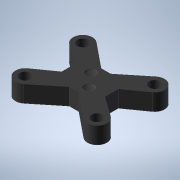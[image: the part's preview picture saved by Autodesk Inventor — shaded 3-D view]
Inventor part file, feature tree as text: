
AUTODESK INVENTOR PART (.ipt)
format: ipt  version: 2021 (Build 250183000, 183)  size: 990,720 bytes
history: native  units: mm
features: other x7, sketch x4, reference x2, extrude x1, mirror x1, plane x1, revolve x1, chamfer x1
ambient origin geometry x8: Origin, YZ Plane, XZ Plane, XY Plane, X Axis, Y Axis, Z Axis, Center Point
bodies: Volumenkörper1 (feature_tree)
feature tree (18):
  other  "Castor_Wheel.ipt"
  extrude  "Extrusion1"  Depth=10.0mm
  mirror  "Spiegeln1"
  sketch  "Skizze2"  dims[d3=4.0mm]
  plane  "Arbeitsebene1"
  sketch  "Skizze4"  dims[d4=10.0mm d5=4.0mm d6=2.0mm d7=2.0mm d8=7.0mm d9=0.0mm d10=60.0deg d11=3.8mm d12=0.6mm d13=3.1505mm d14=0.32475mm d15=0.06495mm d16=60.0deg d17=3.8mm d18=0.6mm d19=3.1505mm d20=0.5196mm d21=0.0mm d22=3.1505mm d23=90.0deg d24=0.6mm d25=7.0mm d26=10.0mm d27=0.0mm d28=90.0deg d29=90.0deg d30=0.0mm d31=0.0mm d32=0.5mm d33=2.0mm d34=45.0deg]
  revolve  "Umdrehung1"
  chamfer  "Fase1"  Distance=4.0mm
  other  "Spirale1"
  sketch  "Skizzenbasierte Anordnung1"  dims[d0=10.0mm d1=0.2mm]
  sketch  "Skizze1"  dims[d2=8.0mm]
  reference  "Referenz1"
  reference  "Referenz2"
  other  "Arbeitsachse1"
  other  "Arbeitsachse2"
  other  "<userpath>\Desktop\Bachelorarbeit\CAD\00_RobotAssembly.iam"
  other  "00_RobotAssembly.iam"
  other  "08_HolderSR04:1"
